# Revit family: IS_Eurovit_V2113_BIM_NL
name_source: partatom
category: Plumbing Fixtures
revit_build: Autodesk Revit MEP 2016 (Build: 20161004_0715(x64)
units: mm (PartAtom-declared; Revit-internal decimal feet)

## family parameters
Always vertical = No
Cut with Voids When Loaded = No
OmniClass Number = 23.45.05.14.14
OmniClass Title = Sinks/Lavatories
Part Type = Normal
Room Calculation Point = No
Round Connector Dimension = Use Diameter
Shared = No
Work Plane-Based = No

## types (1)
- V211301 - EUROVIT HANDWASTAFEL 36X25 1 GAT WIT
    Accessories = www.idealstandardnederland.nl
    AreaUnits = millimeters
    Assembly Code = C1030200
    AssetType = Fixed
    BIMobject category = Basins
    BOSUseNativeGeometries = 1
    BarCode = 8595095901339
    Brand = Ideal Standard
    Brand url = http://www.idealstandard.co.uk
    CodePerformance = DIN EN 14688 CL 25, DIN EN 31
    Color = Wit
    ConnectionType = Sanitair
    CurrencyUnit = Euro
    CurrentRevision = 1
    Description = Eurovit fontein 360 mm van keramiek. 1 kraangat rechts doorgestoken. Exclusief bevestigingsset.
    DurationUnit = jaar
    EAN code = https://8595095901339
    Edition number = 1
    ExpectedLife = 25
    FactoryOfProduction = Teplize
    Features = Fontein 360 mm van keramiek. 1 kraangat rechts doorgestoken. Exclusief bevestigingsset.
    Finish = Wit
    IFC Classification = Sanitary Terminal
    Installation instructions = http://www.idealstandardnederland.nl
    InstallationInstructions = http://www.idealstandardnederland.nl
    LinearUnits = millimeters
    MainColor = Wit
    Manufacturer country = CZ
    Manufacturer name = Ideal Standard
    Material = Keramiek
    Material main = Ceramics
    Model = V211301
    ModelNumber = V211301
    ModelReference = V211301
    Name = EUROVIT HANDWASTAFEL 36X25 1 GAT WIT
    NettWeight = 5,00 KG
    Nominal height = 120
    Nominal width = 360
    NominalHeight = 125 mm  [stored 0.410105 ft]
    NominalLength = 250 mm
    NominalWidth = 360 mm  [stored 1.1811 ft]
    Product Guid = 7a561c20-0c0c-4fc6-9bc3-2e71f0b49324
    Product SKU = V2113
    Product data url = https://bimobject.com
    Product family = EUROVIT
    Product group = Basin
    Product name = EUROVIT HAND RISE BASIN 36X25 1TH
    Product url = http://www.idealstandardnederland.nl
    QR code = http://bimobject.com
    Shape = Gesculptuurd
    Size = 360x250x125 mm
    Space = Internal
    SpareParts = www.idealstandardnederland.nl
    Technical description = http://www.idealstandardnederland.nl
    URL = www.idealstandardnederland.nl
    Uniclass 2.0 Code = PR-35-79-93
    Uniclass 2.0 Description = Wall-Hung Hand Rinse Basins
    Uniclass 2015 Code = Pr_40_20_96_95
    Uniclass 2015 Name = Wall-hung hand rinse basins
    VolumeUnits = liter
    WarrantyDescription = Fabrieksgarantie
    WarrantyDurationParts = 5
    WarrantyDurationUnit = jaar
    Weight Net (Kg) = 6.25

note: [stored X ft] marks values corroborated as IEEE doubles in the binary element streams (Revit-internal decimal feet)

## geometry (parser evidence)
native form markers: Blend x4, Sweep x1
no freeform markers — native parametric forms only
